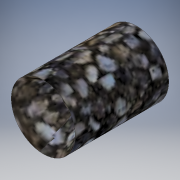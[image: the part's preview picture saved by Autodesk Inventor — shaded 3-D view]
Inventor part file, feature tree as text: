
AUTODESK INVENTOR PART (.ipt)
format: ipt  version: 2019 (Build 230136000, 136)  size: 149,504 bytes
history: native  units: mm
features: revolve x1, sketch x1
ambient origin geometry x8: Origin, YZ Plane, XZ Plane, XY Plane, X Axis, Y Axis, Z Axis, Center Point
bodies: Solid1 (feature_tree)
feature tree (2):
  revolve  "Revolution1"  [1 undecoded]
  sketch  "Sketch1"  dims[d0=15.5mm d3=5.5mm d4=21.816616mm d6=5.0mm d7=29.321531mm d8=11.0mm d9=45.156946mm d10=25.875466mm d11=45.156946mm d12=90.0deg]
note: 1 required parameter value undecoded (feature->parameter linkage not recoverable at this tier; creation-order binding heuristic only, values carry confidence <= 0.55)
